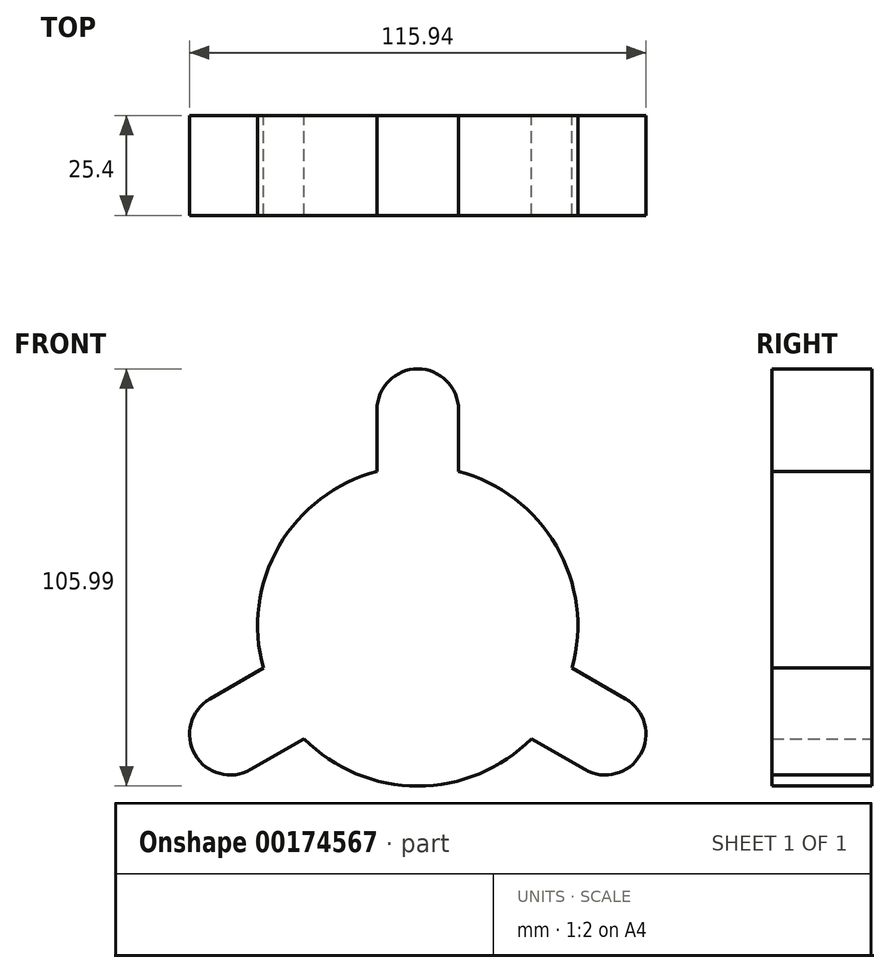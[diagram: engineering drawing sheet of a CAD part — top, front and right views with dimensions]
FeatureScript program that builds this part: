
annotation { "Feature Type Name" : "Feature", "Feature Type Description" : "" }
export const myFeature = defineFeature(function(context is Context, id is Id, definition is map)
    precondition{}
    {
        {
            var Q0;
            Q0=qCreatedBy(makeId("Front.planeOp"),FACE);
            var sketch = newSketch(context, id + "F0", { "sketchPlane" : qUnion([Q0])});
            skPoint(sketch, "E0.center.orphan", {"position": v(-2.45, 0) * mm});
            skArc(sketch, "E1", {"start": v(-10.36, 39.32) * mm, "mid": v(-35.22, 20.33) * mm, "end": v(-39.23, -10.69) * mm});
            skLineSegment(sketch, "E2.left", {"start": v(-10.36, 54.97) * mm, "end": v(-10.36, 39.32) * mm});
            skLineSegment(sketch, "E2.right", {"start": v(10.36, 54.97) * mm, "end": v(10.36, 39.32) * mm});
            skPoint(sketch, "E2.middle", {"position": v(0, 40.66) * mm});
            skArc(sketch, "E3", {"start": v(10.36, 54.97) * mm, "mid": v(0, 65.33) * mm, "end": v(-10.36, 54.97) * mm});
            skPoint(sketch, "E2.top.end.orphan", {"position": v(10.36, 26.36) * mm});
            skPoint(sketch, "E2.top.start.orphan", {"position": v(-10.36, 26.36) * mm});
            skLineSegment(sketch, "E4.1.0", {"start": v(-42.43, -36.46) * mm, "end": v(-28.87, -28.63) * mm});
            skArc(sketch, "E4.1.1", {"start": v(-52.79, -18.51) * mm, "mid": v(-56.58, -32.67) * mm, "end": v(-42.43, -36.46) * mm});
            skLineSegment(sketch, "E4.1.2", {"start": v(-52.79, -18.51) * mm, "end": v(-39.23, -10.69) * mm});
            skLineSegment(sketch, "E4.2.0", {"start": v(52.79, -18.51) * mm, "end": v(39.23, -10.69) * mm});
            skArc(sketch, "E4.2.1", {"start": v(42.43, -36.46) * mm, "mid": v(56.58, -32.67) * mm, "end": v(52.79, -18.51) * mm});
            skLineSegment(sketch, "E4.2.2", {"start": v(42.43, -36.46) * mm, "end": v(28.87, -28.63) * mm});
            skArc(sketch, "E5.trimOffspring", {"start": v(-28.87, -28.63) * mm, "mid": v(0, -40.66) * mm, "end": v(28.87, -28.63) * mm});
            skArc(sketch, "E6.trimOffspring", {"start": v(39.23, -10.69) * mm, "mid": v(35.22, 20.33) * mm, "end": v(10.36, 39.32) * mm});
            skSolve(sketch);
        }
        {
            var Q0;
            Q0 = qSketchRegion(id + "F0", true);
            extrude(context, id + "F1", {"entities" : qUnion([Q0]), "depth" : 25.4 * mm});
        }
    });
